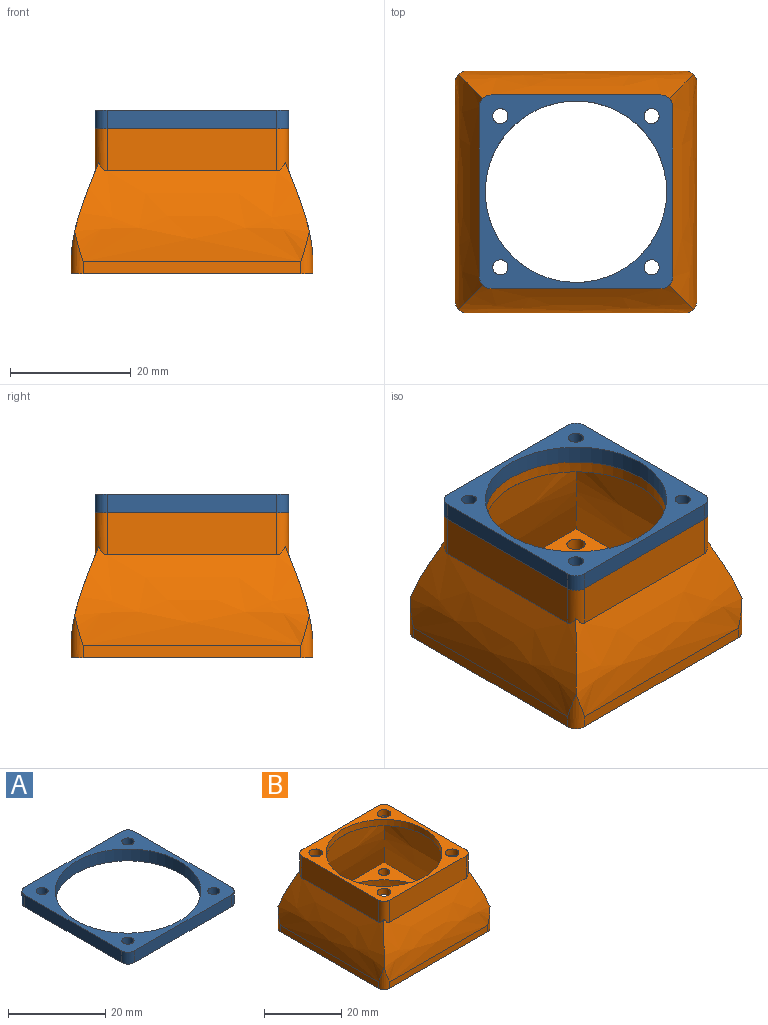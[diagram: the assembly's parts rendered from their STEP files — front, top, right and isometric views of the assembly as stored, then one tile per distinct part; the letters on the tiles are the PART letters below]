
ASSEMBLY  parts=2 mates=1
PART A: 15 faces, bbox 32x32x3 mm
  f0: plane 28.1x3mm, normal (0,-1,0), area 84.3mm2, adj f9,f10,f11,f14
  f1: plane 28.1x3mm, normal (1,0,0), area 84.3mm2, adj f9,f10,f11,f12
  f2: plane 28.1x3mm, normal (0,1,0), area 84.3mm2, adj f9,f10,f12,f13
  f3: cylinder r=15mm len=30mm, axis (0,0,-1), area 282.7mm2, adj f9,f10
  f4: cylinder r=1.25mm len=3mm, axis (0,0,-1), area 23.6mm2, adj f9,f10
  f5: cylinder r=1.25mm len=3mm, axis (0,0,-1), area 23.6mm2, adj f9,f10
  f6: cylinder r=1.25mm len=3mm, axis (0,0,-1), area 23.6mm2, adj f9,f10
  f7: cylinder r=1.25mm len=3mm, axis (0,0,-1), area 23.6mm2, adj f9,f10
  f8: plane 28.1x3mm, normal (-1,0,0), area 84.3mm2, adj f9,f10,f13,f14
  f9: plane 32x32mm, normal (0,0,1), area 294.2mm2, adj f0,f1,f2,f3,f4,f5,f6,f7
  f10: plane 32x32mm, normal (0,0,-1), area 294.2mm2, adj f0,f1,f2,f3,f4,f5,f6,f7
  f11: cylinder r=1.95mm len=3mm, axis (0,0,1), area 9.2mm2, adj f0,f1,f9,f10
  f12: cylinder r=1.95mm len=3mm, axis (0,0,-1), area 9.2mm2, adj f1,f2,f9,f10
  f13: cylinder r=1.95mm len=3mm, axis (0,0,1), area 9.2mm2, adj f2,f8,f9,f10
  f14: cylinder r=1.95mm len=3mm, axis (0,0,-1), area 9.2mm2, adj f0,f8,f9,f10
PART B: 44 faces, bbox 40x40x24 mm
  f0: bspline ~40x16.42mm, area 568.9mm2, adj f1,f3,f6,f22,f37,f38,f42,f43
  f1: bspline ~40x16.42mm, area 568.9mm2, adj f0,f2,f7,f18,f38,f39,f41,f42
  f2: bspline ~40x16.42mm, area 568.9mm2, adj f1,f3,f4,f17,f36,f39,f40,f41
  f3: bspline ~40x16.42mm, area 568.9mm2, adj f0,f2,f5,f16,f36,f37,f40,f43
  f4: plane 28.1x7mm, normal (0,-1,0), area 196.7mm2, adj f2,f34,f36,f39
  f5: plane 28.1x7mm, normal (1,0,0), area 196.7mm2, adj f3,f34,f36,f37
  f6: plane 28.1x7mm, normal (0,1,0), area 196.7mm2, adj f0,f34,f37,f38
  f7: plane 28.1x7mm, normal (-1,0,0), area 196.7mm2, adj f1,f34,f38,f39
  f8: bspline ~38x20mm, area 676.3mm2, adj f9,f11,f12,f13,f26,f27
  f9: bspline ~38x20mm, area 676.3mm2, adj f8,f10,f13,f14,f27,f28
  f10: bspline ~38x20mm, area 676.3mm2, adj f9,f11,f14,f15,f28,f35
  f11: bspline ~38x20mm, area 676.3mm2, adj f8,f10,f12,f15,f26,f35
  f12: plane 19x19mm, normal (0,0,1), area 70.4mm2, adj f8,f11,f19,f23
  f13: plane 19x19mm, normal (0,0,1), area 70.4mm2, adj f8,f9,f23,f24
  f14: plane 19x19mm, normal (0,0,1), area 70.4mm2, adj f9,f10,f21,f23
  f15: plane 19x19mm, normal (0,0,1), area 70.4mm2, adj f10,f11,f20,f23
  f16: plane 36x2mm, normal (1,0,0), area 72mm2, adj f3,f25,f40,f43
  f17: plane 36x2mm, normal (0,-1,0), area 72mm2, adj f2,f25,f40,f41
  f18: plane 36x2mm, normal (-1,0,0), area 72mm2, adj f1,f25,f41,f42
  f19: cylinder r=1.5mm len=3mm, axis (0,0,1), area 18.8mm2, adj f12,f25
  f20: cylinder r=1.5mm len=3mm, axis (0,0,1), area 18.8mm2, adj f15,f25
  f21: cylinder r=1.5mm len=3mm, axis (0,0,1), area 18.8mm2, adj f14,f25
  f22: plane 36x2mm, normal (0,1,0), area 72mm2, adj f0,f25,f42,f43
  f23: cylinder r=19mm len=38mm, axis (0,0,1), area 238.8mm2, adj f12,f13,f14,f15,f25
  f24: cylinder r=1.5mm len=3mm, axis (0,0,1), area 18.8mm2, adj f13,f25
  f25: plane 40x40mm, normal (0,0,-1), area 434.2mm2, adj f16,f17,f18,f19,f20,f21,f22,f23
  f26: plane 15x15mm, normal (0,0,-1), area 38.7mm2, adj f8,f11,f32,f33
  f27: plane 15x15mm, normal (0,0,-1), area 38.7mm2, adj f8,f9,f31,f32
  f28: plane 15x15mm, normal (0,0,-1), area 38.7mm2, adj f9,f10,f30,f32
  f29: cylinder r=1.75mm len=3.5mm, axis (0,0,-1), area 22mm2, adj f34,f35
  f30: cylinder r=1.75mm len=3.5mm, axis (0,0,-1), area 22mm2, adj f28,f34
  f31: cylinder r=1.75mm len=3.5mm, axis (0,0,-1), area 22mm2, adj f27,f34
  f32: cylinder r=15mm len=30mm, axis (0,0,-1), area 188.5mm2, adj f26,f27,f28,f34,f35
  f33: cylinder r=1.75mm len=3.5mm, axis (0,0,-1), area 22mm2, adj f26,f34
  f34: plane 32x32mm, normal (0,0,1), area 275.4mm2, adj f4,f5,f6,f7,f29,f30,f31,f32
  f35: plane 15x15mm, normal (0,0,-1), area 38.7mm2, adj f10,f11,f29,f32
  f36: cylinder r=1.95mm len=7mm, axis (0,0,1), area 20mm2, adj f2,f3,f4,f5,f34
  f37: cylinder r=1.95mm len=7mm, axis (0,0,-1), area 20mm2, adj f0,f3,f5,f6,f34
  f38: cylinder r=1.95mm len=7mm, axis (0,0,1), area 20mm2, adj f0,f1,f6,f7,f34
  f39: cylinder r=1.95mm len=7mm, axis (0,0,-1), area 20mm2, adj f1,f2,f4,f7,f34
  f40: cylinder r=2mm len=6.99mm, axis (0,0,1), area 14.1mm2, adj f2,f3,f16,f17,f25
  f41: cylinder r=2mm len=6.99mm, axis (0,0,1), area 14.1mm2, adj f1,f2,f17,f18,f25
  f42: cylinder r=2mm len=6.99mm, axis (0,0,1), area 14.1mm2, adj f0,f1,f18,f22,f25
  f43: cylinder r=2mm len=6.99mm, axis (0,0,1), area 14.1mm2, adj f0,f3,f16,f22,f25
PLACE A t=(4.6,7.55,26.84)mm
PLACE B t=(4.6,7.55,4.84)mm
MATE fastened A.f7 <-> B.f33  axis (0,0,-1) through (17.1,-4.95,26.84)mm
